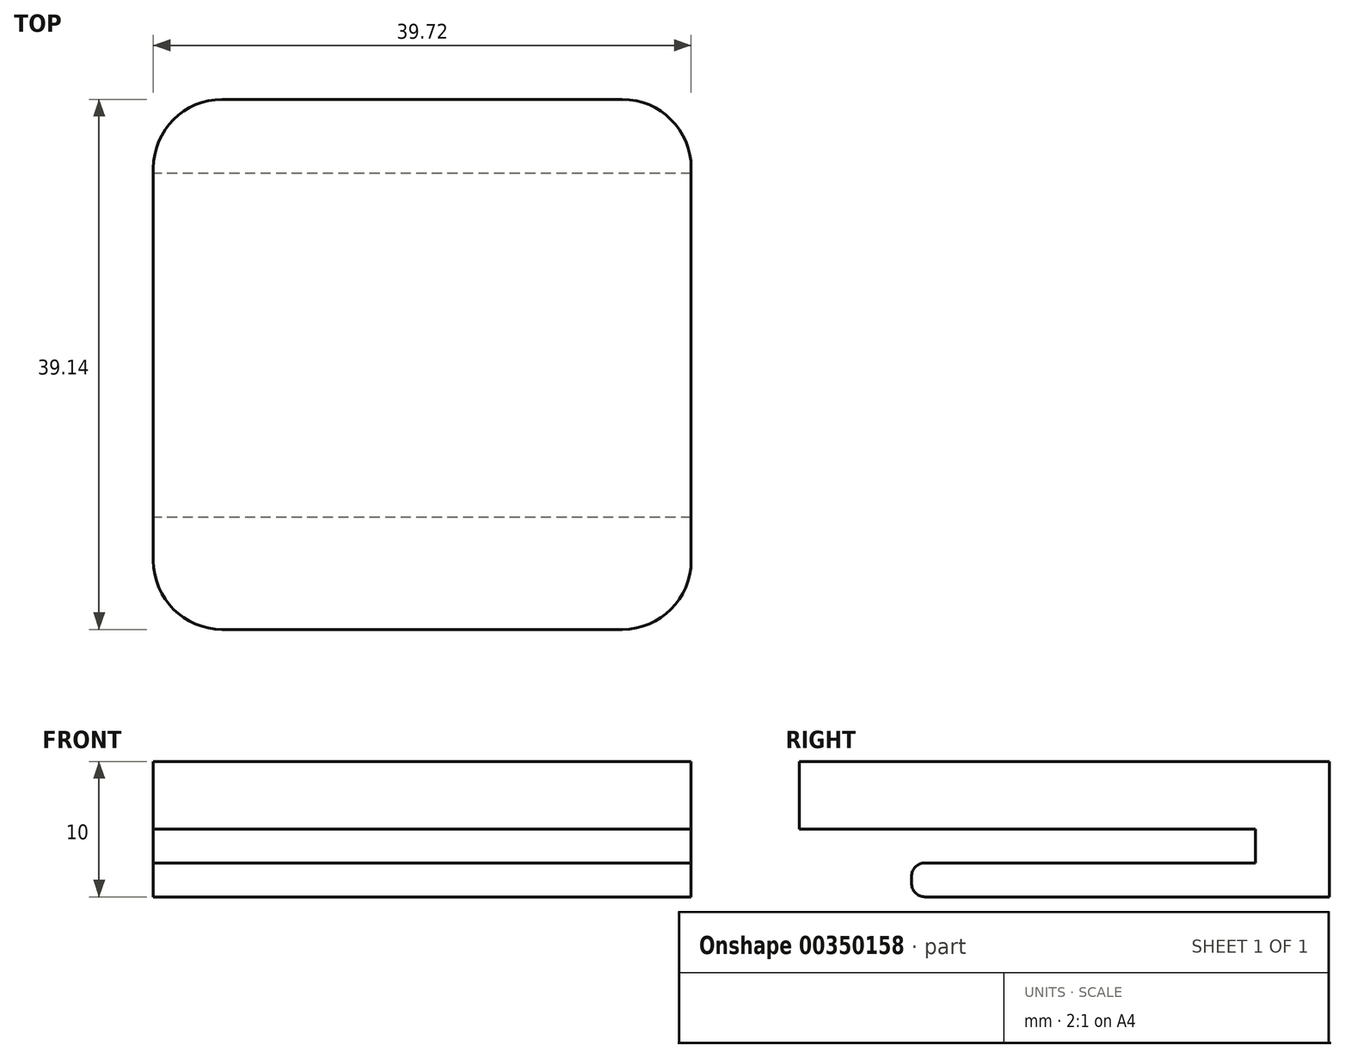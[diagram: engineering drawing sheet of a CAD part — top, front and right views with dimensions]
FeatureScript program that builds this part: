
annotation { "Feature Type Name" : "Feature", "Feature Type Description" : "" }
export const myFeature = defineFeature(function(context is Context, id is Id, definition is map)
    precondition{}
    {
        {
            var Q0;
            Q0=qCreatedBy(makeId("Top.planeOp"),FACE);
            var sketch = newSketch(context, id + "F0", { "sketchPlane" : qUnion([Q0])});
            skLineSegment(sketch, "E0.bottom", {"start": v(-19.86, 19.57) * mm, "end": v(19.86, 19.57) * mm});
            skLineSegment(sketch, "E0.top", {"start": v(-19.86, -19.57) * mm, "end": v(19.86, -19.57) * mm});
            skLineSegment(sketch, "E0.left", {"start": v(-19.86, 19.57) * mm, "end": v(-19.86, -19.57) * mm});
            skLineSegment(sketch, "E0.right", {"start": v(19.86, 19.57) * mm, "end": v(19.86, -19.57) * mm});
            skPoint(sketch, "E0.middle", {"position": v(0, 0) * mm});
            skSolve(sketch);
        }
        {
            var Q0;
            Q0=makeQuery(id+"F0.imprint","IMPRINT",FACE,{"disambiguationData":[TD([[makeQuery(id+"F0.imprint","IMPRINT",EDGE,{"derivedFrom":sQuery(id+"F0.wireOp",EDGE,"E0.bottom")}),-1.0]])]});
            extrude(context, id + "F1", {"entities" : qUnion([Q0]), "depth" : 5 * mm});
        }
        {
            var Q0;
            Q0=makeQuery(id+"F1.opExtrude","CAP_FACE",FACE,{"disambiguationData":[OSD([sQuery(id+"F0.wireOp",EDGE,"E0.bottom"),sQuery(id+"F0.wireOp",EDGE,"E0.top"),sQuery(id+"F0.wireOp",EDGE,"E0.left"),sQuery(id+"F0.wireOp",EDGE,"E0.right")])],"isStart":true});
            var sketch = newSketch(context, id + "F2", { "sketchPlane" : qUnion([Q0])});
            skLineSegment(sketch, "E1.bottom", {"start": v(19.86, -19.57) * mm, "end": v(-19.86, -19.57) * mm});
            skLineSegment(sketch, "E1.top", {"start": v(19.86, -14.1) * mm, "end": v(-19.86, -14.1) * mm});
            skLineSegment(sketch, "E1.left", {"start": v(19.86, -19.57) * mm, "end": v(19.86, -14.1) * mm});
            skLineSegment(sketch, "E1.right", {"start": v(-19.86, -19.57) * mm, "end": v(-19.86, -14.1) * mm});
            skSolve(sketch);
        }
        {
            var Q0;
            Q0=makeQuery(id+"F2.imprint","IMPRINT",FACE,{"disambiguationData":[TD([[makeQuery(id+"F2.imprint","IMPRINT",EDGE,{"derivedFrom":sQuery(id+"F2.wireOp",EDGE,"E1.bottom")}),1.0]])]});
            extrude(context, id + "F3", {"entities" : qUnion([Q0]), "operationType" : NewBodyOperationType.ADD, "depth" : 5 * mm});
        }
        {
            var Q0;
            Q0=makeQuery(id+"F3.opExtrude","SWEPT_FACE",FACE,{"disambiguationData":[OSD([sQuery(id+"F2.wireOp",EDGE,"E1.top")])]});
            var sketch = newSketch(context, id + "F4", { "sketchPlane" : qUnion([Q0])});
            skLineSegment(sketch, "E2.bottom", {"start": v(19.86, -5) * mm, "end": v(-19.86, -5) * mm});
            skLineSegment(sketch, "E2.top", {"start": v(19.86, -2.5) * mm, "end": v(-19.86, -2.5) * mm});
            skLineSegment(sketch, "E2.left", {"start": v(19.86, -5) * mm, "end": v(19.86, -2.5) * mm});
            skLineSegment(sketch, "E2.right", {"start": v(-19.86, -5) * mm, "end": v(-19.86, -2.5) * mm});
            skSolve(sketch);
        }
        {
            var Q0;
            Q0=makeQuery(id+"F4.imprint","IMPRINT",FACE,{"disambiguationData":[TD([[makeQuery(id+"F4.imprint","IMPRINT",EDGE,{"derivedFrom":sQuery(id+"F4.wireOp",EDGE,"E2.bottom")}),-1.0]])]});
            extrude(context, id + "F5", {"entities" : qUnion([Q0]), "operationType" : NewBodyOperationType.ADD, "depth" : 25.4 * mm});
        }
        {
            var Q0;
            Q0=makeQuery(id+"F3.boolean.opBoolean","MERGE",EDGE,{"derivedFrom":[makeQuery(id+"F1.opExtrude","SWEPT_EDGE",EDGE,{"disambiguationData":[OSD([sQuery(id+"F0.wireOp",EDGE,"E0.bottom"),sQuery(id+"F0.wireOp",EDGE,"E0.right")])]}),makeQuery(id+"F3.opExtrude","SWEPT_EDGE",EDGE,{"disambiguationData":[OSD([sQuery(id+"F2.wireOp",EDGE,"E1.bottom"),sQuery(id+"F2.wireOp",EDGE,"E1.left")])]})]});
            var Q1;
            Q1=makeQuery(id+"F1.opExtrude","SWEPT_EDGE",EDGE,{"disambiguationData":[OSD([sQuery(id+"F0.wireOp",EDGE,"E0.top"),sQuery(id+"F0.wireOp",EDGE,"E0.right")])]});
            var Q2;
            Q2=makeQuery(id+"F3.boolean.opBoolean","MERGE",EDGE,{"derivedFrom":[makeQuery(id+"F1.opExtrude","SWEPT_EDGE",EDGE,{"disambiguationData":[OSD([sQuery(id+"F0.wireOp",EDGE,"E0.bottom"),sQuery(id+"F0.wireOp",EDGE,"E0.left")])]}),makeQuery(id+"F3.opExtrude","SWEPT_EDGE",EDGE,{"disambiguationData":[OSD([sQuery(id+"F2.wireOp",EDGE,"E1.bottom"),sQuery(id+"F2.wireOp",EDGE,"E1.right")])]})]});
            var Q3;
            Q3=makeQuery(id+"F1.opExtrude","SWEPT_EDGE",EDGE,{"disambiguationData":[OSD([sQuery(id+"F0.wireOp",EDGE,"E0.top"),sQuery(id+"F0.wireOp",EDGE,"E0.left")])]});
            fillet(context, id + "F6", {"entities" : qUnion([Q0, Q1, Q2, Q3]), "radius" : 5.08 * mm, "tangentPropagation" : true, "allowEdgeOverflow" : false});
        }
        {
            var Q0;
            Q0=makeQuery(id+"F5.opExtrude","CAP_EDGE",EDGE,{"disambiguationData":[OSD([sQuery(id+"F4.wireOp",EDGE,"E2.bottom")])],"isStart":false});
            var Q1;
            Q1=makeQuery(id+"F5.opExtrude","CAP_EDGE",EDGE,{"disambiguationData":[OSD([sQuery(id+"F4.wireOp",EDGE,"E2.top")])],"isStart":false});
            fillet(context, id + "F7", {"entities" : qUnion([Q0, Q1]), "radius" : 1 * mm, "tangentPropagation" : true, "allowEdgeOverflow" : false});
        }
    });
